# Revit family: Lighting_Emergency-Security_Linergy_VIALED-EVO-Emergency-lighting-luminaire
name_source: partatom
category: Lighting Fixtures
revit_build: Autodesk Revit 2018 (Build: 20170223_1515(x64)
units: mm (PartAtom-declared; Revit-internal decimal feet)

## family parameters
Cut with Voids When Loaded = No
Host = Face
Light Source = Yes
OmniClass Number = 23.35.47.13
OmniClass Title = Emergency Lighting
Part Type = Normal
Room Calculation Point = No
Round Connector Dimension = Use Diameter
Shared = No

## types (1)
- Default - please load Revit Family Type Catalog
    Apparent Load = 0 VA
    Apparent Load Phase 2 = 0 VA
    Apparent Load Phase 3 = 0 VA
    Asymmetrical = No
    BIMobject category = Emergency & Security
    Color Filter = 16777215
    Default Elevation = 1219 mm
    Description = LED Emergency lighting luminaire, Recessed on false ceilings, Available in three formats (round shape Ø 85 mm, round shape Ø 68 mm, square shape 59x59 mm), Metal gear in white or grey color, Studied for standard height applications, High lighting peformances, Includes symmetrical and asymmetrical optics
    Design country = Italy
    Detail material = Linergy - Plastic - Polycarbonate Transparent high polished
    Diameter 68mm = Yes
    Diameter 85mm = No
    Dimming Lamp Color Temperature Shift = <None>
    Duration = 1h
    Edition number = 1
    Emit Shape Visible in Rendering = No
    Emit from Circle Diameter = 46 mm  [stored 0.150919 ft]
    Flux M = 360 lm
    Flux N/M = 360 lm
    Function = Rest Mode
    Heat sink material = Linergy - Metal - Zamak
    IFC Classification = Light Fixture
    Input power = 5 VA
    Installation instructions = https://www.linergy.it
    Insulation class = II
    Lamp type = NM/M
    Main material = Linergy - Metal - Steel Powder-coated White RAL 9003
    Manufacturer = Linergy
    Manufacturer country = Italy
    Manufacturer name = Linergy
    Material main = Metal
    Material secondary = Electronic & optical components
    Model = VE1211
    Number of Poles = 1
    OmniClass Code = 23-35 47 13
    OmniClass Description = Emergency Lighting
    Photometric Web File = generic
    Power Factor = 0.0
    Power supply = 230 Vac
    Product Guid = 9f1e3da6-27bb-421d-a328-800c6466864b
    Product SKU = vialed-evo
    Product certification = https://www.linergy.it
    Product data url = https://bimobject.com
    Product family = Emergency luminaires
    Product group = Vialed emergency luminaires
    Product name = VIALED EVO - Emergency lighting luminaire
    Product url = https://www.linergy.it
    Protection degree = IP42
    QR code = https://bimobject.com
    Square = No
    Symmetrical = Yes
    Technical description = https://www.linergy.it
    Tilt Angle = 90.00°
    URL = https://www.linergy.it
    URL - Article page = https://www.linergy.it
    URL - Photometric file (ldt) = https://www.linergy.it
    Voltage = 230 V

note: [stored X ft] marks values corroborated as IEEE doubles in the binary element streams (Revit-internal decimal feet)

## geometry (parser evidence)
native form markers: Sweep x2
no freeform markers — native parametric forms only
